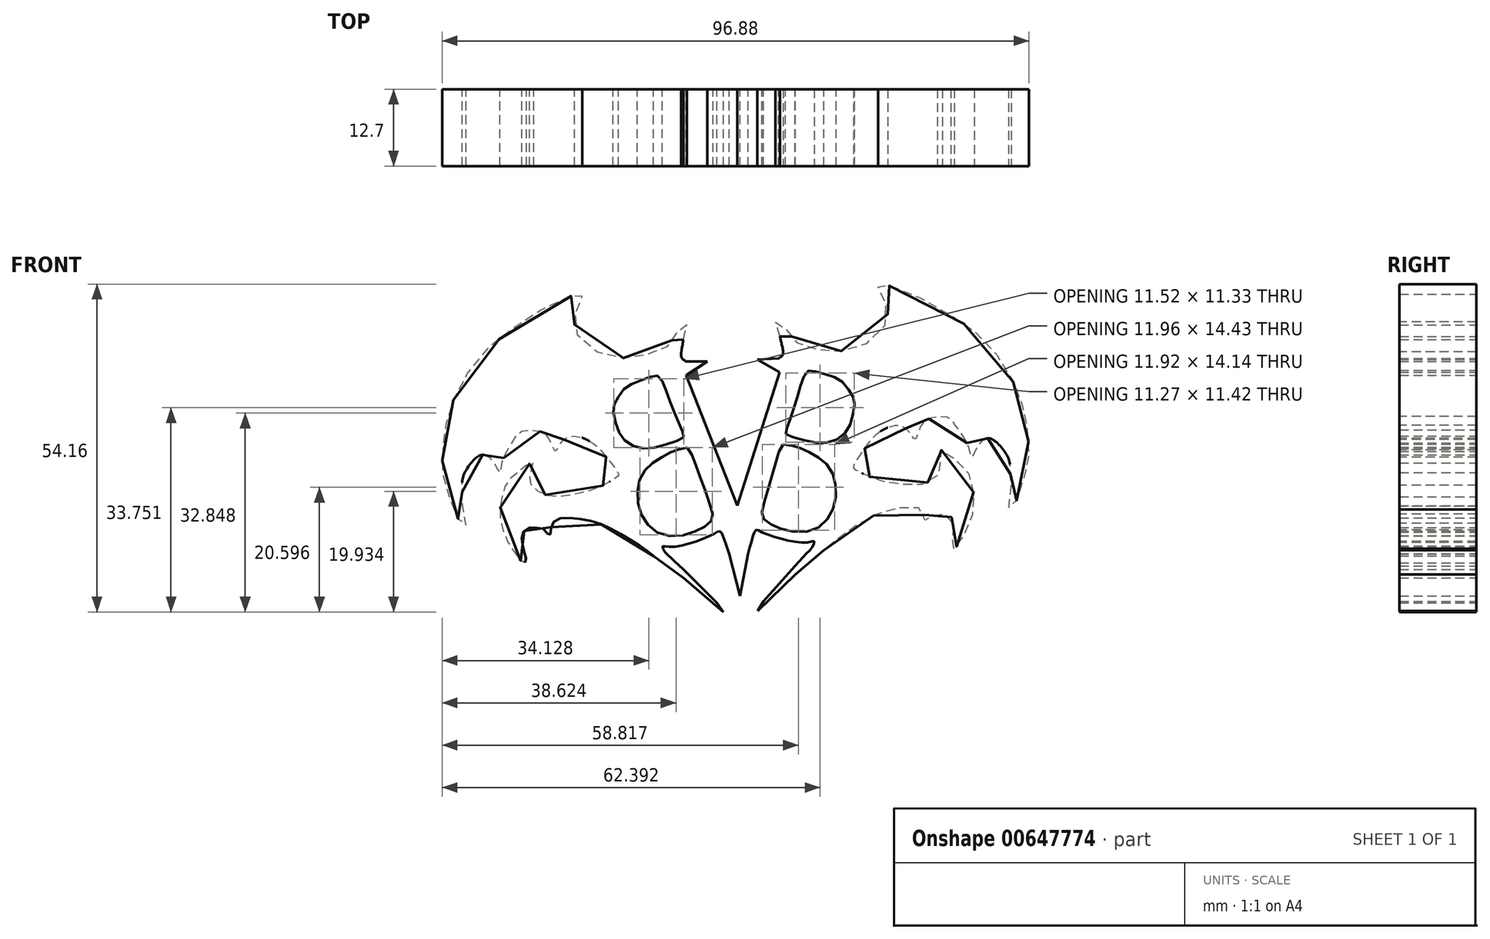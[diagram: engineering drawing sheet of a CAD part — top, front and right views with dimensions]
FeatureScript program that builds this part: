
annotation { "Feature Type Name" : "Feature", "Feature Type Description" : "" }
export const myFeature = defineFeature(function(context is Context, id is Id, definition is map)
    precondition{}
    {
        {
            var Q0;
            Q0=qCreatedBy(makeId("Front.planeOp"),FACE);
            var sketch = newSketch(context, id + "F0", { "sketchPlane" : qUnion([Q0])});
            skLineSegment(sketch, "E0", {"start": v(-8.42, 21.52) * mm, "end": v(0, 0) * mm});
            skLineSegment(sketch, "E1", {"start": v(-8.42, 21.52) * mm, "end": v(-4.92, 23.83) * mm});
            skLineSegment(sketch, "E2", {"start": v(-4.92, 23.83) * mm, "end": v(-8.42, 23.83) * mm});
            skFitSpline(sketch, "E3", {"points": [v(-8.42, 23.83) * mm, v(-9.16, 24.44) * mm, v(-9.05, 26.35) * mm, v(-8.88, 27.41) * mm], "startDerivative": vector(-3.2, 1.45) * mm, "endDerivative": vector(0.42, 3.03) * mm});
            skFitSpline(sketch, "E4", {"points": [v(-8.88, 27.41) * mm, v(-8.43, 28.87) * mm, v(-8.32, 29.83) * mm, v(-8.88, 29.55) * mm, v(-9.9, 28.6) * mm, v(-10.73, 27.41) * mm, v(-11.63, 26.18) * mm, v(-14.04, 25.23) * mm, v(-16.9, 24.33) * mm, v(-20.66, 24.66) * mm, v(-24.48, 26.07) * mm, v(-26.67, 28.87) * mm, v(-26.72, 31.34) * mm, v(-25.94, 33.8) * mm, v(-25.6, 34.7) * mm, v(-26.27, 34.93) * mm, v(-27.23, 34.7) * mm, v(-32.67, 32.13) * mm, v(-38.22, 28.31) * mm, v(-42.04, 25.11) * mm, v(-45.4, 20.34) * mm, v(-47.37, 15.97) * mm, v(-48.15, 13.05) * mm, v(-48.49, 10.75) * mm, v(-48.66, 5.76) * mm, v(-48.04, 3.07) * mm, v(-46.75, -0.75) * mm, v(-45.74, -2.71) * mm, v(-44.95, -3.61) * mm, v(-44.73, -3.05) * mm, v(-45.23, -0.8) * mm, v(-45.35, 2.56) * mm, v(-45.3, 4.52) * mm, v(-44.45, 6.32) * mm, v(-43.05, 7.95) * mm, v(-41.92, 8.4) * mm, v(-40.7, 7.78) * mm, v(-39.51, 5.93) * mm, v(-39.12, 5.42) * mm, v(-38.95, 6.2) * mm, v(-38.17, 8.73) * mm, v(-36.82, 10.86) * mm, v(-35.75, 12.2) * mm, v(-33.23, 12.38) * mm, v(-31.43, 11.6) * mm, v(-30.42, 9.57) * mm, v(-29.98, 8.96) * mm, v(-29.58, 9.57) * mm, v(-28.63, 10.86) * mm, v(-27.45, 11.48) * mm, v(-25.26, 11.09) * mm, v(-23.07, 9.69) * mm, v(-21.11, 7.44) * mm, v(-19.82, 5.7) * mm, v(-19.65, 4.86) * mm, v(-20.66, 4.24) * mm, v(-21.22, 3.8) * mm, v(-24.14, 2.5) * mm, v(-27.11, 1.83) * mm, v(-29.98, 1.44) * mm, v(-32.84, 2.34) * mm, v(-34.18, 4.02) * mm, v(-33.9, 6.1) * mm, v(-33.57, 6.94) * mm, v(-34.24, 6.94) * mm, v(-35.92, 5.7) * mm, v(-37.94, 3.85) * mm, v(-38.95, 0.7) * mm, v(-39.06, -2.26) * mm, v(-38, -5.69) * mm, v(-36.43, -8.21) * mm, v(-35.2, -9.45) * mm, v(-34.8, -9) * mm, v(-35.08, -8.04) * mm, v(-35.42, -6.3) * mm, v(-35.53, -5.07) * mm, v(-34.58, -3.72) * mm, v(-32.72, -3.72) * mm, v(-31.83, -3.95) * mm, v(-30.99, -4.96) * mm, v(-30.82, -4.4) * mm, v(-30.48, -2.94) * mm, v(-29.08, -2.1) * mm, v(-25.66, -2.26) * mm, v(-22.23, -3.16) * mm, v(-18.81, -4.96) * mm, v(-15.56, -6.98) * mm, v(-13.82, -8.32) * mm], "startDerivative": vector(46.65, 143.33) * mm, "endDerivative": vector(134.15, -110.83) * mm});
            skLineSegment(sketch, "E5", {"start": v(-13.82, -8.32) * mm, "end": v(-8.88, -11.97) * mm});
            skLineSegment(sketch, "E6", {"start": v(-8.88, -11.97) * mm, "end": v(-2.26, -17.58) * mm});
            skLineSegment(sketch, "E7", {"start": v(-2.26, -17.58) * mm, "end": v(-3.33, -16.07) * mm});
            skLineSegment(sketch, "E8", {"start": v(-3.33, -16.07) * mm, "end": v(-8.88, -10.57) * mm});
            skFitSpline(sketch, "E9", {"points": [v(-8.88, -10.57) * mm, v(-10.96, -8.6) * mm, v(-11.97, -7.6) * mm, v(-12.3, -6.75) * mm, v(-11.3, -6.8) * mm, v(-7.65, -6.2) * mm, v(-3.83, -4.68) * mm, v(-2.88, -4.23) * mm, v(-2.32, -5.13) * mm, v(-1.3, -8.04) * mm], "startDerivative": vector(-16.77, 16.23) * mm, "endDerivative": vector(7.6, -22.86) * mm});
            skLineSegment(sketch, "E10", {"start": v(-1.3, -8.04) * mm, "end": v(0.49, -14.94) * mm});
            skLineSegment(sketch, "E11", {"start": v(0.49, -14.94) * mm, "end": v(0, 0) * mm});
            skFitSpline(sketch, "E12", {"points": [v(-8.24, 9.57) * mm, v(-7.44, 8.34) * mm, v(-6.6, 6.08) * mm, v(-5.37, 2.68) * mm, v(-4.19, -0.76) * mm, v(-4, -1.99) * mm, v(-4.66, -2.98) * mm, v(-6.26, -3.97) * mm, v(-8.76, -4.87) * mm, v(-12.35, -4.82) * mm, v(-14.75, -3.17) * mm, v(-16.07, -0.8) * mm, v(-16.45, 2.12) * mm, v(-15.93, 4.62) * mm, v(-14.61, 6.5) * mm, v(-12.82, 7.78) * mm, v(-11.03, 8.77) * mm, v(-9.8, 9.24) * mm, v(-8.24, 9.57) * mm]});
            skFitSpline(sketch, "E13", {"points": [v(-8.8, 11.27) * mm, v(-9, 12.21) * mm, v(-9.85, 14.15) * mm, v(-11.22, 17.5) * mm, v(-12.25, 20.28) * mm, v(-13.2, 21.46) * mm, v(-14.47, 21.22) * mm, v(-16.88, 20.33) * mm, v(-18.72, 19.2) * mm, v(-19.94, 17.3) * mm, v(-20.46, 15.9) * mm, v(-19.9, 13.2) * mm, v(-18.9, 11.13) * mm, v(-16.69, 9.66) * mm, v(-13.81, 9.52) * mm, v(-10.56, 10.47) * mm, v(-8.8, 11.27) * mm]});
            skFitSpline(sketch, "E14.MirrorCS", {"points": [v(6.85, 24.33) * mm, v(7.55, 24.99) * mm, v(7.31, 26.88) * mm, v(7.07, 27.93) * mm], "startDerivative": vector(3.1, 1.65) * mm, "endDerivative": vector(-0.62, 3) * mm});
            skLineSegment(sketch, "E15.MirrorCS", {"start": v(7, 22.02) * mm, "end": v(3.36, 24.1) * mm});
            skLineSegment(sketch, "E16.MirrorCS", {"start": v(3.36, 24.1) * mm, "end": v(6.85, 24.33) * mm});
            skLineSegment(sketch, "E17.MirrorCS", {"start": v(14.33, -7.4) * mm, "end": v(9.64, -11.37) * mm});
            skLineSegment(sketch, "E18.MirrorCS", {"start": v(1.83, -7.94) * mm, "end": v(0.49, -14.94) * mm});
            skFitSpline(sketch, "E19.MirrorCS", {"points": [v(9.55, -9.97) * mm, v(11.5, -7.87) * mm, v(12.44, -6.8) * mm, v(12.72, -5.94) * mm, v(11.71, -6.06) * mm, v(8.03, -5.68) * mm, v(4.13, -4.42) * mm, v(3.15, -4.03) * mm, v(2.65, -4.96) * mm, v(1.83, -7.94) * mm], "startDerivative": vector(15.68, 17.28) * mm, "endDerivative": vector(-6.1, -23.3) * mm});
            skLineSegment(sketch, "E20.MirrorCS", {"start": v(4.37, -15.81) * mm, "end": v(9.55, -9.97) * mm});
            skLineSegment(sketch, "E21.MirrorCS", {"start": v(3.4, -17.4) * mm, "end": v(4.37, -15.81) * mm});
            skLineSegment(sketch, "E22.MirrorCS", {"start": v(9.64, -11.37) * mm, "end": v(3.4, -17.4) * mm});
            skFitSpline(sketch, "E23.MirrorC", {"points": [v(7.6, 10.09) * mm, v(6.88, 8.81) * mm, v(6.18, 6.5) * mm, v(5.18, 3.03) * mm, v(4.23, -0.49) * mm, v(4.12, -1.72) * mm, v(4.84, -2.67) * mm, v(6.5, -3.55) * mm, v(9.06, -4.28) * mm, v(12.64, -4) * mm, v(14.93, -2.2) * mm, v(16.1, 0.24) * mm, v(16.28, 3.18) * mm, v(15.6, 5.65) * mm, v(14.16, 7.44) * mm, v(12.29, 8.6) * mm, v(10.43, 9.47) * mm, v(9.18, 9.86) * mm, v(7.6, 10.09) * mm]});
            skFitSpline(sketch, "E24.MirrorCS", {"points": [v(7.07, 27.93) * mm, v(6.53, 29.36) * mm, v(6.36, 30.3) * mm, v(6.94, 30.06) * mm, v(8, 29.18) * mm, v(8.92, 28.05) * mm, v(9.9, 26.88) * mm, v(12.37, 26.09) * mm, v(15.28, 25.38) * mm, v(19, 25.96) * mm, v(22.72, 27.6) * mm, v(24.73, 30.55) * mm, v(24.62, 33.02) * mm, v(23.68, 35.43) * mm, v(23.28, 36.3) * mm, v(23.94, 36.57) * mm, v(24.9, 36.4) * mm, v(30.5, 34.19) * mm, v(36.3, 30.74) * mm, v(40.3, 27.8) * mm, v(43.98, 23.26) * mm, v(46.22, 19.02) * mm, v(47.2, 16.16) * mm, v(47.68, 13.9) * mm, v(48.18, 8.92) * mm, v(47.74, 6.2) * mm, v(46.7, 2.3) * mm, v(45.82, 0.28) * mm, v(45.1, -0.67) * mm, v(44.83, -0.13) * mm, v(45.2, 2.15) * mm, v(45.08, 5.51) * mm, v(44.9, 7.47) * mm, v(43.94, 9.2) * mm, v(42.44, 10.74) * mm, v(41.29, 11.11) * mm, v(40.1, 10.42) * mm, v(39.04, 8.5) * mm, v(38.68, 7.96) * mm, v(38.46, 8.73) * mm, v(37.52, 11.2) * mm, v(36.03, 13.24) * mm, v(34.88, 14.52) * mm, v(32.35, 14.52) * mm, v(30.61, 13.62) * mm, v(29.73, 11.54) * mm, v(29.33, 10.9) * mm, v(28.9, 11.48) * mm, v(27.86, 12.7) * mm, v(26.64, 13.25) * mm, v(24.49, 12.71) * mm, v(22.4, 11.17) * mm, v(20.58, 8.8) * mm, v(19.4, 6.98) * mm, v(19.3, 6.13) * mm, v(20.34, 5.58) * mm, v(20.93, 5.17) * mm, v(23.93, 4.07) * mm, v(26.94, 3.6) * mm, v(29.82, 3.4) * mm, v(32.61, 4.47) * mm, v(33.85, 6.24) * mm, v(33.43, 8.3) * mm, v(33.04, 9.11) * mm, v(33.71, 9.15) * mm, v(35.47, 8.03) * mm, v(37.6, 6.32) * mm, v(38.82, 3.25) * mm, v(39.13, 0.29) * mm, v(38.29, -3.2) * mm, v(36.89, -5.82) * mm, v(35.73, -7.13) * mm, v(35.31, -6.7) * mm, v(35.53, -5.74) * mm, v(35.75, -3.98) * mm, v(35.78, -2.74) * mm, v(34.74, -1.46) * mm, v(32.9, -1.58) * mm, v(32.02, -1.86) * mm, v(31.24, -2.93) * mm, v(31.04, -2.38) * mm, v(30.6, -0.94) * mm, v(29.15, -0.2) * mm, v(25.75, -0.59) * mm, v(22.4, -1.7) * mm, v(19.1, -3.72) * mm, v(15.98, -5.95) * mm, v(14.33, -7.4) * mm], "startDerivative": vector(-55.9, 139.98) * mm, "endDerivative": vector(-126.64, -119.34) * mm});
            skFitSpline(sketch, "E25.MirrorC", {"points": [v(8.06, 11.82) * mm, v(8.18, 12.77) * mm, v(8.9, 14.76) * mm, v(10.05, 18.19) * mm, v(10.9, 21.03) * mm, v(11.77, 22.27) * mm, v(13.06, 22.12) * mm, v(15.52, 21.38) * mm, v(17.42, 20.37) * mm, v(18.77, 18.57) * mm, v(19.38, 17.2) * mm, v(19, 14.47) * mm, v(18.14, 12.34) * mm, v(16.02, 10.73) * mm, v(13.16, 10.4) * mm, v(9.85, 11.13) * mm, v(8.06, 11.82) * mm]});
            skLineSegment(sketch, "E26.MirrorCS", {"start": v(7, 22.02) * mm, "end": v(0, 0) * mm});
            skSolve(sketch);
        }
        {
            var Q0;
            Q0 = qSketchRegion(id + "F0", true);
            extrude(context, id + "F1", {"entities" : qUnion([Q0]), "depth" : 12.7 * mm, "offsetDistance" : 25.4 * mm});
        }
    });
